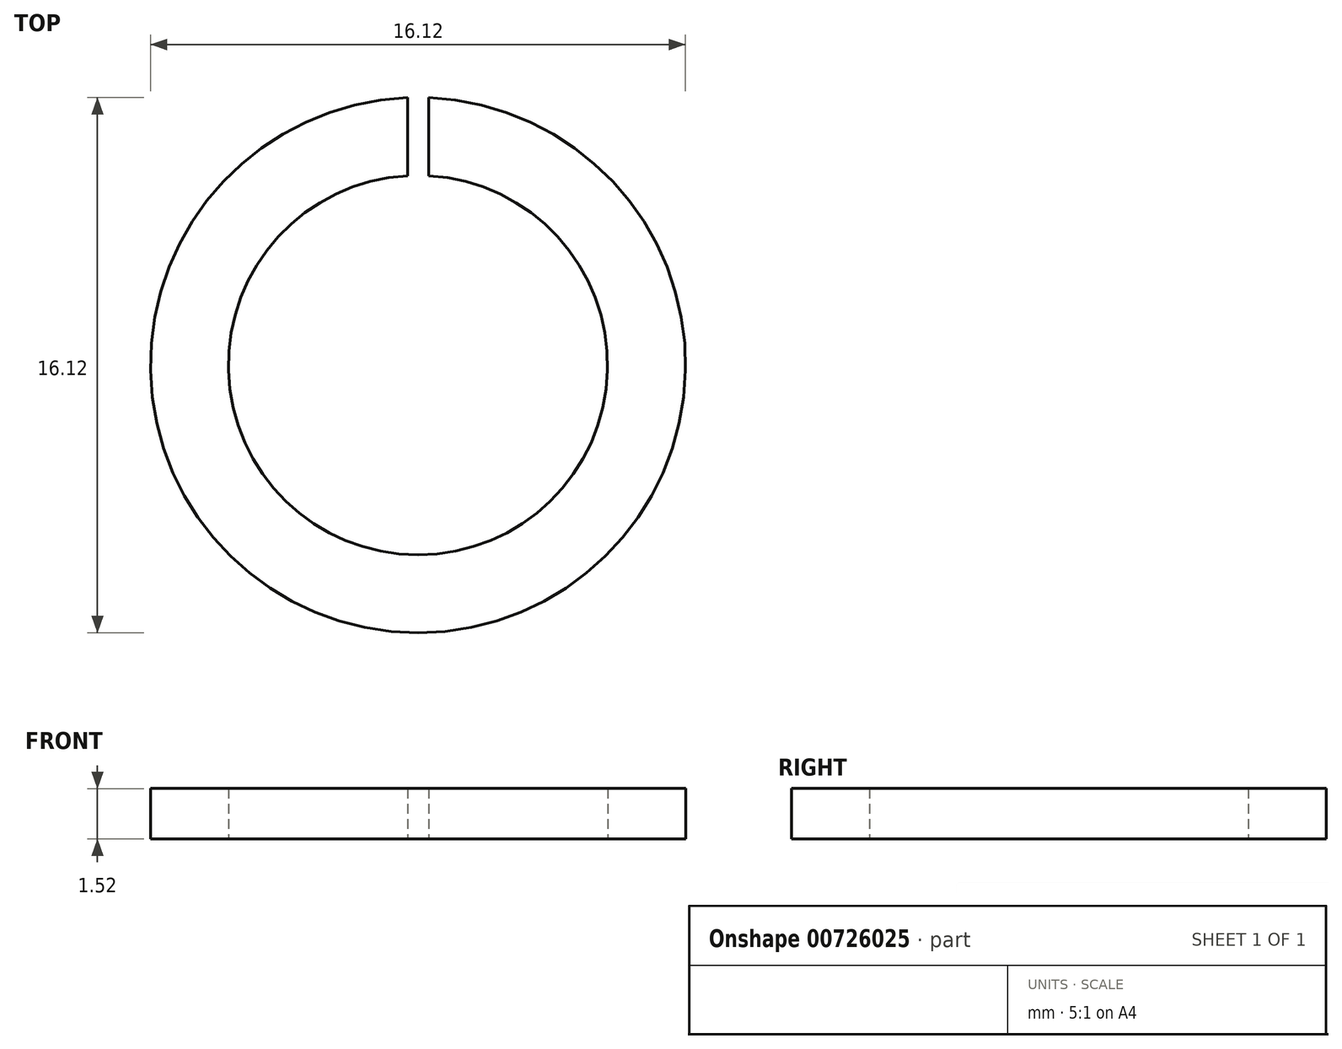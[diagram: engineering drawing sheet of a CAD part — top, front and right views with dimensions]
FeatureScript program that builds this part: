
annotation { "Feature Type Name" : "Feature", "Feature Type Description" : "" }
export const myFeature = defineFeature(function(context is Context, id is Id, definition is map)
    precondition{}
    {
        {
            var Q0;
            Q0=qCreatedBy(makeId("Top.planeOp"),FACE);
            var sketch = newSketch(context, id + "F0", { "sketchPlane" : qUnion([Q0])});
            skCircle(sketch, "E0", {"center": v(0, 0) * mm, "radius": 5.72 * mm});
            skCircle(sketch, "E1", {"center": v(0, 0) * mm, "radius": 8.06 * mm});
            skLineSegment(sketch, "E2.bottom", {"start": v(-0.32, 12.7) * mm, "end": v(0.32, 12.7) * mm});
            skLineSegment(sketch, "E2.top", {"start": v(-0.32, -12.7) * mm, "end": v(0.32, -12.7) * mm});
            skLineSegment(sketch, "E2.left", {"start": v(-0.32, 12.7) * mm, "end": v(-0.32, -12.7) * mm});
            skLineSegment(sketch, "E2.right", {"start": v(0.32, 12.7) * mm, "end": v(0.32, -12.7) * mm});
            skSolve(sketch);
        }
        {
            var Q0;
            {var subQ0=sQuery(id+"F0.wireOp",EDGE,"E2.left");var subQ1=sQuery(id+"F0.wireOp",EDGE,"E0");var subQ2=makeQuery(id+"F0.imprint","INTERSECT",VERTEX,{"disambiguationData":[OD(0.0)],"derivedFrom":[subQ1,subQ0]});Q0=makeQuery(id+"F0.imprint","IMPRINT",FACE,{"disambiguationData":[TD([[makeQuery(id+"F0.imprint","IMPRINT",EDGE,{"disambiguationData":[TD([[subQ2,-1.0]])],"derivedFrom":subQ1}),-1.0]])]});}
            var Q1;
            {var subQ0=sQuery(id+"F0.wireOp",EDGE,"E2.left");var subQ1=sQuery(id+"F0.wireOp",EDGE,"E0");var subQ2=makeQuery(id+"F0.imprint","INTERSECT",VERTEX,{"disambiguationData":[OD(1.0)],"derivedFrom":[subQ1,subQ0]});Q1=makeQuery(id+"F0.imprint","IMPRINT",FACE,{"disambiguationData":[TD([[makeQuery(id+"F0.imprint","IMPRINT",EDGE,{"disambiguationData":[TD([[subQ2,-1.0]])],"derivedFrom":subQ1}),-1.0]])]});}
            var Q2;
            {var subQ0=sQuery(id+"F0.wireOp",EDGE,"E2.right");var subQ1=sQuery(id+"F0.wireOp",EDGE,"E0");var subQ2=makeQuery(id+"F0.imprint","INTERSECT",VERTEX,{"disambiguationData":[OD(0.0)],"derivedFrom":[subQ1,subQ0]});Q2=makeQuery(id+"F0.imprint","IMPRINT",FACE,{"disambiguationData":[TD([[makeQuery(id+"F0.imprint","IMPRINT",EDGE,{"disambiguationData":[TD([[subQ2,1.0]])],"derivedFrom":subQ1}),-1.0]])]});}
            var Q3;
            {var subQ0=sQuery(id+"F0.wireOp",EDGE,"E2.left");var subQ1=sQuery(id+"F0.wireOp",EDGE,"E1");var subQ2=makeQuery(id+"F0.imprint","INTERSECT",VERTEX,{"disambiguationData":[OD(1.0)],"derivedFrom":[subQ1,subQ0]});Q3=makeQuery(id+"F0.imprint","IMPRINT",FACE,{"disambiguationData":[TD([[makeQuery(id+"F0.imprint","IMPRINT",EDGE,{"disambiguationData":[TD([[subQ2,-1.0]])],"derivedFrom":subQ1}),1.0]])]});}
            var Q4;
            {var subQ0=sQuery(id+"F0.wireOp",EDGE,"zKp1Jdg5-SP03-cKtQ-K927-zFCOivq8ji5k.bottom");var subQ1=sQuery(id+"F0.wireOp",EDGE,"E1");var subQ2=makeQuery(id+"F0.imprint","INTERSECT",VERTEX,{"disambiguationData":[OD(0.0)],"derivedFrom":[subQ1,subQ0]});Q4=makeQuery(id+"F0.imprint","IMPRINT",FACE,{"disambiguationData":[TD([[makeQuery(id+"F0.imprint","IMPRINT",EDGE,{"disambiguationData":[TD([[subQ2,-1.0]])],"derivedFrom":subQ1}),1.0]])]});}
            var Q5;
            {var subQ0=sQuery(id+"F0.wireOp",EDGE,"E2.right");var subQ1=sQuery(id+"F0.wireOp",EDGE,"E1");var subQ2=makeQuery(id+"F0.imprint","INTERSECT",VERTEX,{"disambiguationData":[OD(1.0)],"derivedFrom":[subQ1,subQ0]});Q5=makeQuery(id+"F0.imprint","IMPRINT",FACE,{"disambiguationData":[TD([[makeQuery(id+"F0.imprint","IMPRINT",EDGE,{"disambiguationData":[TD([[subQ2,-1.0]])],"derivedFrom":subQ1}),1.0]])]});}
            extrude(context, id + "F1", {"entities" : qUnion([Q0, Q1, Q2, Q3, Q4, Q5]), "depth" : 1.52 * mm, "offsetDistance" : 25.4 * mm});
        }
    });
